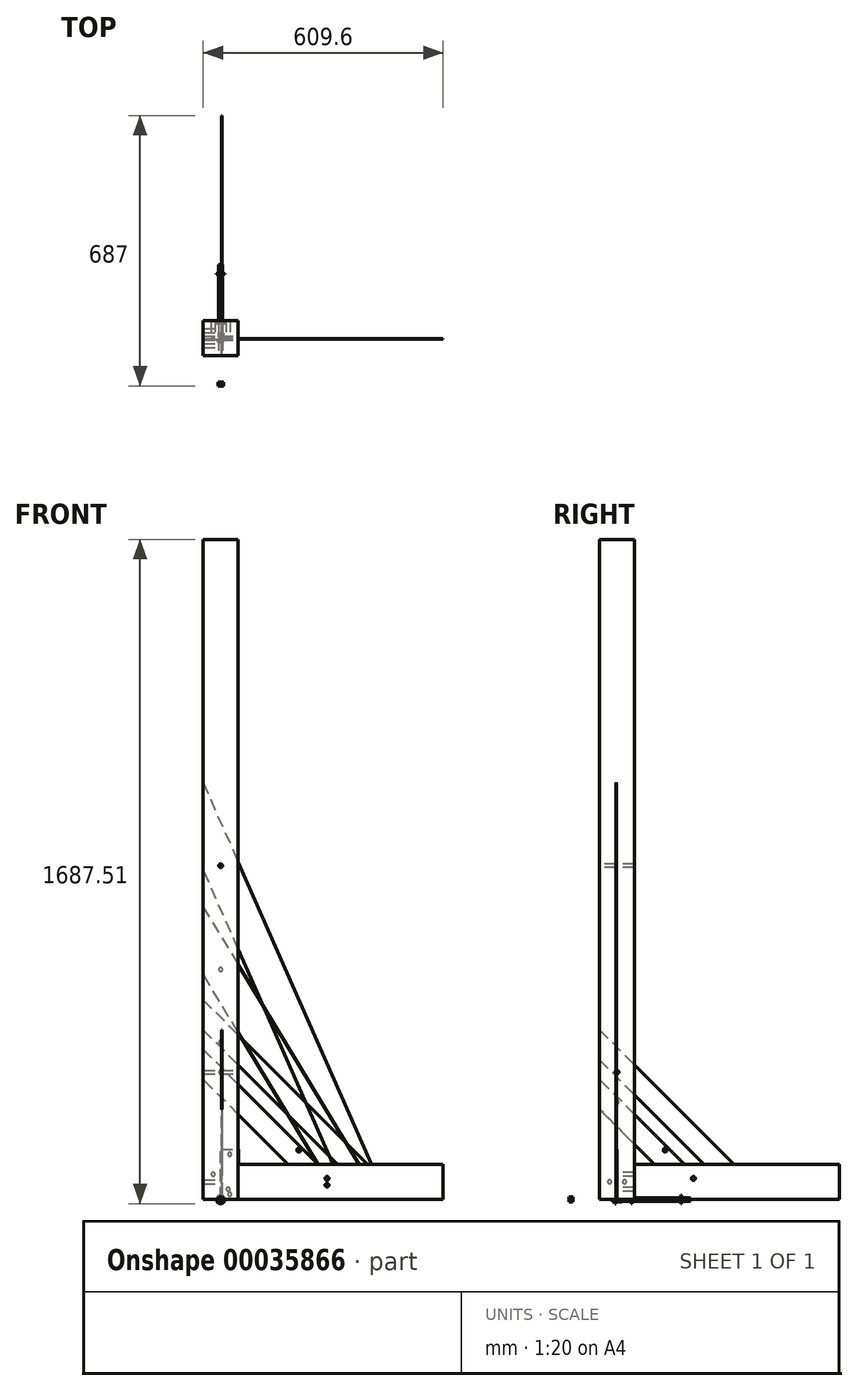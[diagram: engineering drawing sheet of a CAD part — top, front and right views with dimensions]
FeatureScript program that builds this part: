
annotation { "Feature Type Name" : "Feature", "Feature Type Description" : "" }
export const myFeature = defineFeature(function(context is Context, id is Id, definition is map)
    precondition{}
    {
        {
            assignVariable(context, id + "F0", {"name" : "mscthick", "anyValue" : 3.5});
        }
        {
            assignVariable(context, id + "F1", {"name" : "basethick", "anyValue" : 1.5});
        }
        {
            assignVariable(context, id + "F2", {"name" : "msc6", "anyValue" : 152.4 * mm});
        }
        {
            assignVariable(context, id + "F3", {"name" : "msc18", "anyValue" : 457.2 * mm});
        }
        {
            assignVariable(context, id + "F4", {"name" : "msc45", "anyValue" : 1143 * mm});
        }
        {
            assignVariable(context, id + "F5", {"name" : "msc24", "anyValue" : 609.6 * mm});
        }
        {
            assignVariable(context, id + "F6", {"name" : "msc30", "anyValue" : 762 * mm});
        }
        {
            assignVariable(context, id + "F7", {"name" : "msc66", "anyValue" : 1676.4 * mm});
        }
        {
            var Q0;
            Q0=qCreatedBy(makeId("Front.planeOp"),FACE);
            cPlane(context, id + "F8", {"entities" : qUnion([Q0]), "cplaneType" : CPlaneType.OFFSET, "offset" : (getVariable(context, 'mscthick') / 2) * mm, "width" : 152.4 * mm, "height" : 152.4 * mm});
        }
        {
            var Q0;
            Q0=qCreatedBy(makeId("Front.planeOp"),FACE);
            cPlane(context, id + "F9", {"entities" : qUnion([Q0]), "cplaneType" : CPlaneType.OFFSET, "offset" : (getVariable(context, 'mscthick') / 2) * mm, "oppositeDirection" : true, "width" : 152.4 * mm, "height" : 152.4 * mm});
        }
        {
            var Q0;
            Q0=qCreatedBy(makeId("Right.planeOp"),FACE);
            cPlane(context, id + "F10", {"entities" : qUnion([Q0]), "cplaneType" : CPlaneType.OFFSET, "offset" : (getVariable(context, 'mscthick') / 2) * mm, "width" : 152.4 * mm, "height" : 152.4 * mm});
        }
        {
            var Q0;
            Q0=qCreatedBy(makeId("Right.planeOp"),FACE);
            cPlane(context, id + "F11", {"entities" : qUnion([Q0]), "cplaneType" : CPlaneType.OFFSET, "offset" : (getVariable(context, 'mscthick') / 2) * mm, "oppositeDirection" : true, "width" : 152.4 * mm, "height" : 152.4 * mm});
        }
        {
            var Q0;
            Q0=qCreatedBy(id+"F8.planeOp",FACE);
            cPlane(context, id + "F12", {"entities" : qUnion([Q0]), "cplaneType" : CPlaneType.OFFSET, "offset" : (getVariable(context, 'basethick')) * mm, "width" : 152.4 * mm, "height" : 152.4 * mm});
        }
        {
            var Q0;
            Q0=qCreatedBy(id+"F9.planeOp",FACE);
            cPlane(context, id + "F13", {"entities" : qUnion([Q0]), "cplaneType" : CPlaneType.OFFSET, "offset" : (getVariable(context, 'basethick')) * mm, "oppositeDirection" : true, "width" : 152.4 * mm, "height" : 152.4 * mm});
        }
        {
            var Q0;
            Q0=qCreatedBy(id+"F10.planeOp",FACE);
            cPlane(context, id + "F14", {"entities" : qUnion([Q0]), "cplaneType" : CPlaneType.OFFSET, "offset" : (getVariable(context, 'basethick')) * mm, "width" : 152.4 * mm, "height" : 152.4 * mm});
        }
        {
            var Q0;
            Q0=qCreatedBy(makeId("Top.planeOp"),FACE);
            var sketch = newSketch(context, id + "F15", { "sketchPlane" : qUnion([Q0])});
            skLineSegment(sketch, "E0.rect.bottom", {"start": v(44.45, -44.45) * mm, "end": v(-44.45, -44.45) * mm});
            skLineSegment(sketch, "E0.rect.top", {"start": v(44.45, 44.45) * mm, "end": v(-44.45, 44.45) * mm});
            skLineSegment(sketch, "E0.rect.left", {"start": v(44.45, -44.45) * mm, "end": v(44.45, 44.45) * mm});
            skLineSegment(sketch, "E0.rect.right", {"start": v(-44.45, -44.45) * mm, "end": v(-44.45, 44.45) * mm});
            skPoint(sketch, "E0.rect.middle", {"position": v(0, 0) * mm});
            skSolve(sketch);
        }
        {
            var Q0;
            Q0=qCreatedBy(id+"F8.planeOp",FACE);
            var sketch = newSketch(context, id + "F16", { "sketchPlane" : qUnion([Q0])});
            skLineSegment(sketch, "E1", {"start": v(0, 0) * mm, "end": v(0, 88.9) * mm, "construction": true});
            skLineSegment(sketch, "E2.rect.bottom", {"start": v(44.45, 0) * mm, "end": v(-44.45, 0) * mm, "construction": true});
            skLineSegment(sketch, "E2.rect.top", {"start": v(44.45, 88.9) * mm, "end": v(-44.45, 88.9) * mm, "construction": true});
            skLineSegment(sketch, "E2.rect.left", {"start": v(44.45, 0) * mm, "end": v(44.45, 88.9) * mm, "construction": true});
            skLineSegment(sketch, "E2.rect.right", {"start": v(-44.45, 0) * mm, "end": v(-44.45, 88.9) * mm, "construction": true});
            skPoint(sketch, "E2.rect.middle", {"position": v(0, 44.45) * mm});
            skLineSegment(sketch, "E3.bottom", {"start": v(-44.45, 88.9) * mm, "end": v(-19.05, 88.9) * mm, "construction": true});
            skLineSegment(sketch, "E3.top", {"start": v(-44.45, 63.5) * mm, "end": v(-19.05, 63.5) * mm, "construction": true});
            skLineSegment(sketch, "E3.left", {"start": v(-44.45, 88.9) * mm, "end": v(-44.45, 63.5) * mm, "construction": true});
            skLineSegment(sketch, "E3.right", {"start": v(-19.05, 88.9) * mm, "end": v(-19.05, 63.5) * mm, "construction": true});
            skLineSegment(sketch, "E4.bottom", {"start": v(44.45, 0) * mm, "end": v(19.05, 0) * mm, "construction": true});
            skLineSegment(sketch, "E4.top", {"start": v(44.45, 25.4) * mm, "end": v(19.05, 25.4) * mm, "construction": true});
            skLineSegment(sketch, "E4.left", {"start": v(44.45, 0) * mm, "end": v(44.45, 25.4) * mm, "construction": true});
            skLineSegment(sketch, "E4.right", {"start": v(19.05, 0) * mm, "end": v(19.05, 25.4) * mm, "construction": true});
            skCircle(sketch, "E5", {"center": v(-19.05, 63.5) * mm, "radius": 4.76 * mm});
            skCircle(sketch, "E6", {"center": v(19.05, 25.4) * mm, "radius": 4.76 * mm});
            skSolve(sketch);
        }
        {
            var Q0;
            Q0=qCreatedBy(id+"F10.planeOp",FACE);
            var sketch = newSketch(context, id + "F17", { "sketchPlane" : qUnion([Q0])});
            skLineSegment(sketch, "E7", {"start": v(0, 0) * mm, "end": v(0, 88.9) * mm, "construction": true});
            skLineSegment(sketch, "E8.rect.bottom", {"start": v(44.45, 0) * mm, "end": v(-44.45, 0) * mm, "construction": true});
            skLineSegment(sketch, "E8.rect.top", {"start": v(44.45, 88.9) * mm, "end": v(-44.45, 88.9) * mm, "construction": true});
            skLineSegment(sketch, "E8.rect.left", {"start": v(44.45, 0) * mm, "end": v(44.45, 88.9) * mm, "construction": true});
            skLineSegment(sketch, "E8.rect.right", {"start": v(-44.45, 0) * mm, "end": v(-44.45, 88.9) * mm, "construction": true});
            skPoint(sketch, "E8.rect.middle", {"position": v(0, 44.45) * mm});
            skLineSegment(sketch, "E9", {"start": v(-44.45, 44.45) * mm, "end": v(-19.05, 44.45) * mm, "construction": true});
            skPoint(sketch, "E9.endSnap0", {"position": v(44.45, 44.45) * mm});
            skLineSegment(sketch, "E10", {"start": v(-19.05, 44.45) * mm, "end": v(19.05, 44.45) * mm, "construction": true});
            skLineSegment(sketch, "E11", {"start": v(19.05, 44.45) * mm, "end": v(44.45, 44.45) * mm, "construction": true});
            skCircle(sketch, "E12", {"center": v(-19.05, 44.45) * mm, "radius": 4.76 * mm});
            skCircle(sketch, "E13", {"center": v(19.05, 44.45) * mm, "radius": 4.76 * mm});
            skSolve(sketch);
        }
        {
            var Q0;
            Q0=qCreatedBy(id+"F8.planeOp",FACE);
            var sketch = newSketch(context, id + "F18", { "sketchPlane" : qUnion([Q0])});
            skLineSegment(sketch, "E14", {"start": v(0, 0) * mm, "end": v(-44.45, 0) * mm, "construction": true});
            skLineSegment(sketch, "E15", {"start": v(-44.45, 0) * mm, "end": v(-44.45, 88.9) * mm, "construction": true});
            skLineSegment(sketch, "E16.bottom", {"start": v(-44.45, 0) * mm, "end": v(565.15, 0) * mm});
            skLineSegment(sketch, "E16.top", {"start": v(-44.45, 88.9) * mm, "end": v(565.15, 88.9) * mm});
            skLineSegment(sketch, "E16.left", {"start": v(-44.45, 0) * mm, "end": v(-44.45, 88.9) * mm});
            skLineSegment(sketch, "E16.right", {"start": v(565.15, 0) * mm, "end": v(565.15, 88.9) * mm});
            skLineSegment(sketch, "E17.bottom", {"start": v(-44.45, 88.9) * mm, "end": v(-19.05, 88.9) * mm, "construction": true});
            skLineSegment(sketch, "E17.top", {"start": v(-44.45, 63.5) * mm, "end": v(-19.05, 63.5) * mm, "construction": true});
            skLineSegment(sketch, "E17.left", {"start": v(-44.45, 88.9) * mm, "end": v(-44.45, 63.5) * mm, "construction": true});
            skLineSegment(sketch, "E17.right", {"start": v(-19.05, 88.9) * mm, "end": v(-19.05, 63.5) * mm, "construction": true});
            skLineSegment(sketch, "E18", {"start": v(-44.45, 88.9) * mm, "end": v(44.45, 0) * mm, "construction": true});
            skLineSegment(sketch, "E19.bottom", {"start": v(44.45, 0) * mm, "end": v(19.05, 0) * mm, "construction": true});
            skLineSegment(sketch, "E19.top", {"start": v(44.45, 25.4) * mm, "end": v(19.05, 25.4) * mm, "construction": true});
            skLineSegment(sketch, "E19.left", {"start": v(44.45, 0) * mm, "end": v(44.45, 25.4) * mm, "construction": true});
            skLineSegment(sketch, "E19.right", {"start": v(19.05, 0) * mm, "end": v(19.05, 25.4) * mm, "construction": true});
            skCircle(sketch, "E20", {"center": v(-19.05, 63.5) * mm, "radius": 4.76 * mm});
            skCircle(sketch, "E21", {"center": v(19.05, 25.4) * mm, "radius": 4.76 * mm});
            skSolve(sketch);
        }
        {
            var Q0;
            Q0=qCreatedBy(id+"F10.planeOp",FACE);
            var sketch = newSketch(context, id + "F19", { "sketchPlane" : qUnion([Q0])});
            skLineSegment(sketch, "E22", {"start": v(0, 0) * mm, "end": v(-44.45, 0) * mm, "construction": true});
            skLineSegment(sketch, "E23", {"start": v(-44.45, 0) * mm, "end": v(-44.45, 88.9) * mm, "construction": true});
            skLineSegment(sketch, "E24.bottom", {"start": v(-44.45, 88.9) * mm, "end": v(565.15, 88.9) * mm});
            skLineSegment(sketch, "E24.top", {"start": v(-44.45, 0) * mm, "end": v(565.15, 0) * mm});
            skLineSegment(sketch, "E24.left", {"start": v(-44.45, 88.9) * mm, "end": v(-44.45, 0) * mm});
            skLineSegment(sketch, "E24.right", {"start": v(565.15, 88.9) * mm, "end": v(565.15, 0) * mm});
            skLineSegment(sketch, "E25", {"start": v(0, 0) * mm, "end": v(0, 88.9) * mm, "construction": true});
            skLineSegment(sketch, "E26", {"start": v(-44.45, 44.45) * mm, "end": v(-19.05, 44.45) * mm, "construction": true});
            skLineSegment(sketch, "E27", {"start": v(-19.05, 44.45) * mm, "end": v(19.05, 44.45) * mm, "construction": true});
            skLineSegment(sketch, "E28", {"start": v(19.05, 44.45) * mm, "end": v(44.45, 44.45) * mm, "construction": true});
            skCircle(sketch, "E29", {"center": v(-19.05, 44.45) * mm, "radius": 4.76 * mm});
            skCircle(sketch, "E30", {"center": v(19.05, 44.45) * mm, "radius": 4.76 * mm});
            skSolve(sketch);
        }
        {
            var Q0;
            Q0=qCreatedBy(id+"F14.planeOp",FACE);
            var sketch = newSketch(context, id + "F20", { "sketchPlane" : qUnion([Q0])});
            skLineSegment(sketch, "E31", {"start": v(171.45, 0) * mm, "end": v(-44.45, 0) * mm, "construction": true});
            skLineSegment(sketch, "E32", {"start": v(-44.45, 0) * mm, "end": v(-44.45, 304.8) * mm, "construction": true});
            skLineSegment(sketch, "E33", {"start": v(-44.45, 304.8) * mm, "end": v(171.45, 88.9) * mm, "construction": true});
            skLineSegment(sketch, "E34", {"start": v(171.45, 88.9) * mm, "end": v(171.45, 0) * mm, "construction": true});
            skLineSegment(sketch, "E35", {"start": v(171.45, 0) * mm, "end": v(260.35, 0) * mm, "construction": true});
            skLineSegment(sketch, "E36", {"start": v(63.5, 196.85) * mm, "end": v(126.36, 259.71) * mm, "construction": true});
            skLineSegment(sketch, "E37", {"start": v(126.36, 259.71) * mm, "end": v(-44.45, 430.52) * mm, "construction": true});
            skLineSegment(sketch, "E38", {"start": v(-44.45, 304.8) * mm, "end": v(-44.45, 430.52) * mm});
            skLineSegment(sketch, "E39", {"start": v(-44.45, 430.52) * mm, "end": v(297.17, 88.9) * mm});
            skLineSegment(sketch, "E40", {"start": v(297.17, 88.9) * mm, "end": v(171.45, 88.9) * mm});
            skLineSegment(sketch, "E41", {"start": v(171.45, 88.9) * mm, "end": v(-44.45, 304.8) * mm});
            skLineSegment(sketch, "E42", {"start": v(-44.45, 367.66) * mm, "end": v(234.31, 88.9) * mm, "construction": true});
            skLineSegment(sketch, "E43", {"start": v(0, 0) * mm, "end": v(0, 365.42) * mm, "construction": true});
            skLineSegment(sketch, "E44.rect.bottom", {"start": v(25.4, 297.81) * mm, "end": v(-25.4, 297.81) * mm, "construction": true});
            skLineSegment(sketch, "E44.rect.top", {"start": v(25.4, 348.61) * mm, "end": v(-25.4, 348.61) * mm, "construction": true});
            skLineSegment(sketch, "E44.rect.left", {"start": v(25.4, 297.81) * mm, "end": v(25.4, 348.61) * mm, "construction": true});
            skLineSegment(sketch, "E44.rect.right", {"start": v(-25.4, 297.81) * mm, "end": v(-25.4, 348.61) * mm, "construction": true});
            skPoint(sketch, "E44.rect.middle", {"position": v(0, 323.21) * mm});
            skCircle(sketch, "E45", {"center": v(0, 323.21) * mm, "radius": 4.76 * mm});
            skSolve(sketch);
        }
        {
            var Q0;
            Q0=qCreatedBy(makeId("Right.planeOp"),FACE);
            var sketch = newSketch(context, id + "F21", { "sketchPlane" : qUnion([Q0])});
            skLineSegment(sketch, "E46", {"start": v(171.45, 0) * mm, "end": v(-44.45, 0) * mm, "construction": true});
            skLineSegment(sketch, "E47", {"start": v(-44.45, 0) * mm, "end": v(-44.45, 304.8) * mm, "construction": true});
            skLineSegment(sketch, "E48", {"start": v(-44.45, 304.8) * mm, "end": v(171.45, 88.9) * mm, "construction": true});
            skLineSegment(sketch, "E49", {"start": v(171.45, 88.9) * mm, "end": v(171.45, 0) * mm, "construction": true});
            skLineSegment(sketch, "E50", {"start": v(171.45, 0) * mm, "end": v(260.35, 0) * mm, "construction": true});
            skLineSegment(sketch, "E51", {"start": v(63.5, 196.85) * mm, "end": v(126.36, 259.71) * mm, "construction": true});
            skLineSegment(sketch, "E52", {"start": v(126.36, 259.71) * mm, "end": v(-44.45, 430.52) * mm, "construction": true});
            skLineSegment(sketch, "E53", {"start": v(-44.45, 304.8) * mm, "end": v(-44.45, 430.52) * mm, "construction": true});
            skLineSegment(sketch, "E54", {"start": v(-44.45, 430.52) * mm, "end": v(297.17, 88.9) * mm, "construction": true});
            skLineSegment(sketch, "E55", {"start": v(297.17, 88.9) * mm, "end": v(171.45, 88.9) * mm, "construction": true});
            skLineSegment(sketch, "E56", {"start": v(171.45, 88.9) * mm, "end": v(-44.45, 304.8) * mm, "construction": true});
            skLineSegment(sketch, "E57", {"start": v(-44.45, 367.66) * mm, "end": v(234.31, 88.9) * mm, "construction": true});
            skLineSegment(sketch, "E58", {"start": v(0, 0) * mm, "end": v(0, 142.77) * mm, "construction": true});
            skLineSegment(sketch, "E59.rect.bottom", {"start": v(25.4, 297.81) * mm, "end": v(-25.4, 297.81) * mm, "construction": true});
            skLineSegment(sketch, "E59.rect.top", {"start": v(25.4, 348.61) * mm, "end": v(-25.4, 348.61) * mm, "construction": true});
            skLineSegment(sketch, "E59.rect.left", {"start": v(25.4, 297.81) * mm, "end": v(25.4, 348.61) * mm, "construction": true});
            skLineSegment(sketch, "E59.rect.right", {"start": v(-25.4, 297.81) * mm, "end": v(-25.4, 348.61) * mm, "construction": true});
            skPoint(sketch, "E59.rect.middle", {"position": v(0, 323.21) * mm});
            skCircle(sketch, "E60", {"center": v(0, 323.21) * mm, "radius": 4.76 * mm});
            skSolve(sketch);
        }
        {
            var Q0;
            Q0=qCreatedBy(makeId("Front.planeOp"),FACE);
            var sketch = newSketch(context, id + "F22", { "sketchPlane" : qUnion([Q0])});
            skLineSegment(sketch, "E61", {"start": v(95.25, 0) * mm, "end": v(-44.45, 0) * mm, "construction": true});
            skLineSegment(sketch, "E62", {"start": v(-44.45, 0) * mm, "end": v(-44.45, 228.6) * mm, "construction": true});
            skLineSegment(sketch, "E63", {"start": v(-44.45, 228.6) * mm, "end": v(95.25, 88.9) * mm, "construction": true});
            skLineSegment(sketch, "E64", {"start": v(95.25, 88.9) * mm, "end": v(95.25, 0) * mm, "construction": true});
            skLineSegment(sketch, "E65", {"start": v(95.25, 0) * mm, "end": v(184.15, 0) * mm, "construction": true});
            skLineSegment(sketch, "E66", {"start": v(201.17, 108.7) * mm, "end": v(-44.45, 354.32) * mm, "construction": true});
            skLineSegment(sketch, "E67", {"start": v(-44.45, 228.6) * mm, "end": v(-44.45, 354.32) * mm, "construction": true});
            skLineSegment(sketch, "E68", {"start": v(-44.45, 354.32) * mm, "end": v(220.97, 88.9) * mm, "construction": true});
            skLineSegment(sketch, "E69", {"start": v(220.97, 88.9) * mm, "end": v(95.25, 88.9) * mm, "construction": true});
            skLineSegment(sketch, "E70", {"start": v(95.25, 88.9) * mm, "end": v(-44.45, 228.6) * mm, "construction": true});
            skLineSegment(sketch, "E71", {"start": v(-44.45, 291.46) * mm, "end": v(158.11, 88.9) * mm, "construction": true});
            skLineSegment(sketch, "E72", {"start": v(0, 0) * mm, "end": v(0, 309.87) * mm, "construction": true});
            skLineSegment(sketch, "E73.rect.bottom", {"start": v(25.4, 221.61) * mm, "end": v(-25.4, 221.61) * mm, "construction": true});
            skLineSegment(sketch, "E73.rect.top", {"start": v(25.4, 272.41) * mm, "end": v(-25.4, 272.41) * mm, "construction": true});
            skLineSegment(sketch, "E73.rect.left", {"start": v(25.4, 221.61) * mm, "end": v(25.4, 272.41) * mm, "construction": true});
            skLineSegment(sketch, "E73.rect.right", {"start": v(-25.4, 221.61) * mm, "end": v(-25.4, 272.41) * mm, "construction": true});
            skPoint(sketch, "E73.rect.middle", {"position": v(0, 247.01) * mm});
            skCircle(sketch, "E74", {"center": v(0, 247.01) * mm, "radius": 4.76 * mm});
            skSolve(sketch);
        }
        {
            var Q0;
            Q0=qCreatedBy(id+"F8.planeOp",FACE);
            var sketch = newSketch(context, id + "F23", { "sketchPlane" : qUnion([Q0])});
            skLineSegment(sketch, "E75", {"start": v(171.45, 0) * mm, "end": v(-44.45, 0) * mm, "construction": true});
            skLineSegment(sketch, "E76", {"start": v(-44.45, 0) * mm, "end": v(-44.45, 304.8) * mm, "construction": true});
            skLineSegment(sketch, "E77", {"start": v(-44.45, 304.8) * mm, "end": v(171.45, 88.9) * mm, "construction": true});
            skLineSegment(sketch, "E78", {"start": v(171.45, 88.9) * mm, "end": v(171.45, 0) * mm, "construction": true});
            skLineSegment(sketch, "E79", {"start": v(171.45, 0) * mm, "end": v(260.35, 0) * mm, "construction": true});
            skLineSegment(sketch, "E80", {"start": v(63.5, 196.85) * mm, "end": v(126.36, 259.71) * mm, "construction": true});
            skLineSegment(sketch, "E81", {"start": v(126.36, 259.71) * mm, "end": v(-44.45, 430.52) * mm, "construction": true});
            skLineSegment(sketch, "E82", {"start": v(-44.45, 304.8) * mm, "end": v(-44.45, 430.52) * mm});
            skLineSegment(sketch, "E83", {"start": v(-44.45, 430.52) * mm, "end": v(297.17, 88.9) * mm});
            skLineSegment(sketch, "E84", {"start": v(297.17, 88.9) * mm, "end": v(171.45, 88.9) * mm});
            skLineSegment(sketch, "E85", {"start": v(171.45, 88.9) * mm, "end": v(-44.45, 304.8) * mm});
            skLineSegment(sketch, "E86", {"start": v(-44.45, 367.66) * mm, "end": v(234.31, 88.9) * mm, "construction": true});
            skLineSegment(sketch, "E87", {"start": v(0, 0) * mm, "end": v(0, 594.1) * mm, "construction": true});
            skLineSegment(sketch, "E88.rect.bottom", {"start": v(25.4, 297.81) * mm, "end": v(-25.4, 297.81) * mm, "construction": true});
            skLineSegment(sketch, "E88.rect.top", {"start": v(25.4, 348.61) * mm, "end": v(-25.4, 348.61) * mm, "construction": true});
            skLineSegment(sketch, "E88.rect.left", {"start": v(25.4, 297.81) * mm, "end": v(25.4, 348.61) * mm, "construction": true});
            skLineSegment(sketch, "E88.rect.right", {"start": v(-25.4, 297.81) * mm, "end": v(-25.4, 348.61) * mm, "construction": true});
            skPoint(sketch, "E88.rect.middle", {"position": v(0, 323.21) * mm});
            skCircle(sketch, "E89", {"center": v(0, 323.21) * mm, "radius": 4.76 * mm});
            skSolve(sketch);
        }
        {
            var Q0;
            Q0=qCreatedBy(id+"F14.planeOp",FACE);
            var sketch = newSketch(context, id + "F24", { "sketchPlane" : qUnion([Q0])});
            skLineSegment(sketch, "E90", {"start": v(95.25, 0) * mm, "end": v(-44.45, 0) * mm, "construction": true});
            skLineSegment(sketch, "E91", {"start": v(-44.45, 0) * mm, "end": v(-44.45, 228.6) * mm, "construction": true});
            skLineSegment(sketch, "E92", {"start": v(-44.45, 228.6) * mm, "end": v(95.25, 88.9) * mm, "construction": true});
            skLineSegment(sketch, "E93", {"start": v(95.25, 88.9) * mm, "end": v(95.25, 0) * mm, "construction": true});
            skLineSegment(sketch, "E94", {"start": v(95.25, 0) * mm, "end": v(184.15, 0) * mm, "construction": true});
            skLineSegment(sketch, "E95", {"start": v(201.17, 108.7) * mm, "end": v(-44.45, 354.32) * mm, "construction": true});
            skLineSegment(sketch, "E96", {"start": v(-44.45, 228.6) * mm, "end": v(-44.45, 354.32) * mm});
            skLineSegment(sketch, "E97", {"start": v(-44.45, 354.32) * mm, "end": v(220.97, 88.9) * mm});
            skLineSegment(sketch, "E98", {"start": v(220.97, 88.9) * mm, "end": v(95.25, 88.9) * mm});
            skLineSegment(sketch, "E99", {"start": v(95.25, 88.9) * mm, "end": v(-44.45, 228.6) * mm});
            skLineSegment(sketch, "E100", {"start": v(-44.45, 291.46) * mm, "end": v(158.11, 88.9) * mm, "construction": true});
            skLineSegment(sketch, "E101", {"start": v(0, 0) * mm, "end": v(0, 309.87) * mm, "construction": true});
            skLineSegment(sketch, "E102.rect.bottom", {"start": v(25.4, 221.61) * mm, "end": v(-25.4, 221.61) * mm, "construction": true});
            skLineSegment(sketch, "E102.rect.top", {"start": v(25.4, 272.41) * mm, "end": v(-25.4, 272.41) * mm, "construction": true});
            skLineSegment(sketch, "E102.rect.left", {"start": v(25.4, 221.61) * mm, "end": v(25.4, 272.41) * mm, "construction": true});
            skLineSegment(sketch, "E102.rect.right", {"start": v(-25.4, 221.61) * mm, "end": v(-25.4, 272.41) * mm, "construction": true});
            skPoint(sketch, "E102.rect.middle", {"position": v(0, 247.01) * mm});
            skCircle(sketch, "E103", {"center": v(0, 247.01) * mm, "radius": 4.76 * mm});
            skSolve(sketch);
        }
        {
            var Q0;
            Q0=qCreatedBy(makeId("Front.planeOp"),FACE);
            var sketch = newSketch(context, id + "F25", { "sketchPlane" : qUnion([Q0])});
            skLineSegment(sketch, "E104", {"start": v(0, 0) * mm, "end": v(-44.45, 0) * mm, "construction": true});
            skLineSegment(sketch, "E105", {"start": v(-44.45, 0) * mm, "end": v(-44.45, 304.8) * mm, "construction": true});
            skLineSegment(sketch, "E106", {"start": v(-44.45, 0) * mm, "end": v(260.35, 0) * mm, "construction": true});
            skLineSegment(sketch, "E107", {"start": v(260.35, 0) * mm, "end": v(171.45, 0) * mm, "construction": true});
            skLineSegment(sketch, "E108", {"start": v(171.45, 0) * mm, "end": v(171.45, 88.9) * mm, "construction": true});
            skLineSegment(sketch, "E109", {"start": v(171.45, 88.9) * mm, "end": v(-44.45, 304.8) * mm, "construction": true});
            skLineSegment(sketch, "E110", {"start": v(-44.45, 304.8) * mm, "end": v(-44.45, 430.52) * mm, "construction": true});
            skLineSegment(sketch, "E111", {"start": v(-44.45, 430.52) * mm, "end": v(297.17, 88.9) * mm, "construction": true});
            skLineSegment(sketch, "E112", {"start": v(297.17, 88.9) * mm, "end": v(171.45, 88.9) * mm, "construction": true});
            skLineSegment(sketch, "E113", {"start": v(-44.45, 367.66) * mm, "end": v(234.31, 88.9) * mm, "construction": true});
            skLineSegment(sketch, "E114", {"start": v(0, 0) * mm, "end": v(0, 386.07) * mm, "construction": true});
            skPoint(sketch, "E115.rect.middle", {"position": v(0, 323.21) * mm});
            skCircle(sketch, "E116", {"center": v(0, 323.21) * mm, "radius": 4.76 * mm});
            skSolve(sketch);
        }
        {
            var Q0;
            Q0=qCreatedBy(makeId("Right.planeOp"),FACE);
            var sketch = newSketch(context, id + "F26", { "sketchPlane" : qUnion([Q0])});
            skLineSegment(sketch, "E117", {"start": v(95.25, 0) * mm, "end": v(-44.45, 0) * mm, "construction": true});
            skLineSegment(sketch, "E118", {"start": v(-44.45, 0) * mm, "end": v(-44.45, 228.6) * mm, "construction": true});
            skLineSegment(sketch, "E119", {"start": v(-44.45, 228.6) * mm, "end": v(95.25, 88.9) * mm, "construction": true});
            skLineSegment(sketch, "E120", {"start": v(95.25, 88.9) * mm, "end": v(95.25, 0) * mm, "construction": true});
            skLineSegment(sketch, "E121", {"start": v(95.25, 0) * mm, "end": v(184.15, 0) * mm, "construction": true});
            skLineSegment(sketch, "E122", {"start": v(201.17, 108.7) * mm, "end": v(-44.45, 354.32) * mm, "construction": true});
            skLineSegment(sketch, "E123", {"start": v(-44.45, 228.6) * mm, "end": v(-44.45, 354.32) * mm, "construction": true});
            skLineSegment(sketch, "E124", {"start": v(-44.45, 354.32) * mm, "end": v(220.97, 88.9) * mm, "construction": true});
            skLineSegment(sketch, "E125", {"start": v(220.97, 88.9) * mm, "end": v(95.25, 88.9) * mm, "construction": true});
            skLineSegment(sketch, "E126", {"start": v(95.25, 88.9) * mm, "end": v(-44.45, 228.6) * mm, "construction": true});
            skLineSegment(sketch, "E127", {"start": v(-44.45, 291.46) * mm, "end": v(158.11, 88.9) * mm, "construction": true});
            skLineSegment(sketch, "E128", {"start": v(0, 0) * mm, "end": v(0, 309.87) * mm, "construction": true});
            skLineSegment(sketch, "E129.rect.bottom", {"start": v(25.4, 221.61) * mm, "end": v(-25.4, 221.61) * mm, "construction": true});
            skLineSegment(sketch, "E129.rect.top", {"start": v(25.4, 272.41) * mm, "end": v(-25.4, 272.41) * mm, "construction": true});
            skLineSegment(sketch, "E129.rect.left", {"start": v(25.4, 221.61) * mm, "end": v(25.4, 272.41) * mm, "construction": true});
            skLineSegment(sketch, "E129.rect.right", {"start": v(-25.4, 221.61) * mm, "end": v(-25.4, 272.41) * mm, "construction": true});
            skPoint(sketch, "E129.rect.middle", {"position": v(0, 247.01) * mm});
            skCircle(sketch, "E130", {"center": v(0, 247.01) * mm, "radius": 4.76 * mm});
            skSolve(sketch);
        }
        {
            var Q0;
            Q0=qCreatedBy(id+"F8.planeOp",FACE);
            var sketch = newSketch(context, id + "F27", { "sketchPlane" : qUnion([Q0])});
            skLineSegment(sketch, "E131", {"start": v(-44.45, 0) * mm, "end": v(336.55, 0) * mm, "construction": true});
            skLineSegment(sketch, "E132", {"start": v(247.65, 0) * mm, "end": v(247.65, 88.9) * mm, "construction": true});
            skLineSegment(sketch, "E133", {"start": v(-44.45, 0) * mm, "end": v(-44.45, 381) * mm, "construction": true});
            skLineSegment(sketch, "E134", {"start": v(-44.45, 381) * mm, "end": v(247.65, 88.9) * mm});
            skLineSegment(sketch, "E135", {"start": v(-44.45, 506.72) * mm, "end": v(373.37, 88.9) * mm});
            skLineSegment(sketch, "E136", {"start": v(373.37, 88.9) * mm, "end": v(247.65, 88.9) * mm});
            skLineSegment(sketch, "E137", {"start": v(-44.45, 381) * mm, "end": v(-44.45, 506.72) * mm});
            skLineSegment(sketch, "E138", {"start": v(0, 0) * mm, "end": v(0, 462.27) * mm, "construction": true});
            skLineSegment(sketch, "E139", {"start": v(-44.45, 443.86) * mm, "end": v(310.51, 88.9) * mm, "construction": true});
            skLineSegment(sketch, "E140.rect.bottom", {"start": v(25.4, 374.01) * mm, "end": v(-25.4, 374.01) * mm, "construction": true});
            skLineSegment(sketch, "E140.rect.top", {"start": v(25.4, 424.81) * mm, "end": v(-25.4, 424.81) * mm, "construction": true});
            skLineSegment(sketch, "E140.rect.left", {"start": v(25.4, 374.01) * mm, "end": v(25.4, 424.81) * mm, "construction": true});
            skLineSegment(sketch, "E140.rect.right", {"start": v(-25.4, 374.01) * mm, "end": v(-25.4, 424.81) * mm, "construction": true});
            skPoint(sketch, "E140.rect.middle", {"position": v(0, 399.41) * mm});
            skCircle(sketch, "E141", {"center": v(0, 399.41) * mm, "radius": 4.76 * mm});
            skSolve(sketch);
        }
        {
            var Q0;
            Q0=qCreatedBy(makeId("Front.planeOp"),FACE);
            var sketch = newSketch(context, id + "F28", { "sketchPlane" : qUnion([Q0])});
            skLineSegment(sketch, "E142", {"start": v(-44.45, 0) * mm, "end": v(336.55, 0) * mm, "construction": true});
            skLineSegment(sketch, "E143", {"start": v(247.65, 0) * mm, "end": v(247.65, 88.9) * mm, "construction": true});
            skLineSegment(sketch, "E144", {"start": v(-44.45, 0) * mm, "end": v(-44.45, 381) * mm, "construction": true});
            skLineSegment(sketch, "E145", {"start": v(-44.45, 381) * mm, "end": v(247.65, 88.9) * mm, "construction": true});
            skLineSegment(sketch, "E146", {"start": v(-44.45, 506.72) * mm, "end": v(373.37, 88.9) * mm, "construction": true});
            skLineSegment(sketch, "E147", {"start": v(373.37, 88.9) * mm, "end": v(247.65, 88.9) * mm, "construction": true});
            skLineSegment(sketch, "E148", {"start": v(-44.45, 381) * mm, "end": v(-44.45, 506.72) * mm, "construction": true});
            skLineSegment(sketch, "E149", {"start": v(0, 0) * mm, "end": v(0, 462.27) * mm, "construction": true});
            skLineSegment(sketch, "E150", {"start": v(-44.45, 443.86) * mm, "end": v(310.51, 88.9) * mm, "construction": true});
            skLineSegment(sketch, "E151.rect.bottom", {"start": v(25.4, 374.01) * mm, "end": v(-25.4, 374.01) * mm, "construction": true});
            skLineSegment(sketch, "E151.rect.top", {"start": v(25.4, 424.81) * mm, "end": v(-25.4, 424.81) * mm, "construction": true});
            skLineSegment(sketch, "E151.rect.left", {"start": v(25.4, 374.01) * mm, "end": v(25.4, 424.81) * mm, "construction": true});
            skLineSegment(sketch, "E151.rect.right", {"start": v(-25.4, 374.01) * mm, "end": v(-25.4, 424.81) * mm, "construction": true});
            skPoint(sketch, "E151.rect.middle", {"position": v(0, 399.41) * mm});
            skCircle(sketch, "E152", {"center": v(-25.4, 424.81) * mm, "radius": 4.76 * mm, "construction": true});
            skCircle(sketch, "E153", {"center": v(25.4, 374.01) * mm, "radius": 4.76 * mm, "construction": true});
            skCircle(sketch, "E154", {"center": v(-25.4, 374.01) * mm, "radius": 4.76 * mm, "construction": true});
            skCircle(sketch, "E155", {"center": v(25.4, 424.81) * mm, "radius": 4.76 * mm, "construction": true});
            skCircle(sketch, "E156", {"center": v(0, 399.41) * mm, "radius": 4.76 * mm});
            skSolve(sketch);
        }
        {
            var Q0;
            Q0=qCreatedBy(id+"F12.planeOp",FACE);
            var sketch = newSketch(context, id + "F29", { "sketchPlane" : qUnion([Q0])});
            skLineSegment(sketch, "E157", {"start": v(247.65, 0) * mm, "end": v(-44.45, 0) * mm, "construction": true});
            skLineSegment(sketch, "E158", {"start": v(-44.45, 0) * mm, "end": v(-44.45, 571.5) * mm, "construction": true});
            skLineSegment(sketch, "E159", {"start": v(-44.45, 571.5) * mm, "end": v(247.65, 88.9) * mm, "construction": true});
            skLineSegment(sketch, "E160", {"start": v(247.65, 88.9) * mm, "end": v(247.65, 0) * mm, "construction": true});
            skLineSegment(sketch, "E161", {"start": v(247.65, 0) * mm, "end": v(336.55, 0) * mm, "construction": true});
            skLineSegment(sketch, "E162", {"start": v(250.83, 255.33) * mm, "end": v(-44.45, 743.19) * mm, "construction": true});
            skLineSegment(sketch, "E163", {"start": v(-44.45, 571.5) * mm, "end": v(-44.45, 743.19) * mm});
            skLineSegment(sketch, "E164", {"start": v(-44.45, 743.19) * mm, "end": v(351.57, 88.9) * mm});
            skLineSegment(sketch, "E165", {"start": v(351.57, 88.9) * mm, "end": v(247.65, 88.9) * mm});
            skLineSegment(sketch, "E166", {"start": v(247.65, 88.9) * mm, "end": v(-44.45, 571.5) * mm});
            skLineSegment(sketch, "E167", {"start": v(-44.45, 657.34) * mm, "end": v(299.6, 88.9) * mm, "construction": true});
            skLineSegment(sketch, "E168", {"start": v(0, 0) * mm, "end": v(0, 669.75) * mm, "construction": true});
            skLineSegment(sketch, "E169.rect.bottom", {"start": v(25.4, 541.94) * mm, "end": v(-25.4, 541.94) * mm, "construction": true});
            skLineSegment(sketch, "E169.rect.top", {"start": v(25.4, 625.87) * mm, "end": v(-25.4, 625.87) * mm, "construction": true});
            skLineSegment(sketch, "E169.rect.left", {"start": v(25.4, 541.94) * mm, "end": v(25.4, 625.87) * mm, "construction": true});
            skLineSegment(sketch, "E169.rect.right", {"start": v(-25.4, 541.94) * mm, "end": v(-25.4, 625.87) * mm, "construction": true});
            skPoint(sketch, "E169.rect.middle", {"position": v(0, 583.9) * mm});
            skCircle(sketch, "E170", {"center": v(0, 583.9) * mm, "radius": 4.76 * mm});
            skSolve(sketch);
        }
        {
            var Q0;
            Q0=qCreatedBy(makeId("Front.planeOp"),FACE);
            var sketch = newSketch(context, id + "F30", { "sketchPlane" : qUnion([Q0])});
            skLineSegment(sketch, "E171", {"start": v(247.65, 0) * mm, "end": v(-44.45, 0) * mm, "construction": true});
            skLineSegment(sketch, "E172", {"start": v(-44.45, 0) * mm, "end": v(-44.45, 571.5) * mm, "construction": true});
            skLineSegment(sketch, "E173", {"start": v(-44.45, 571.5) * mm, "end": v(247.65, 88.9) * mm, "construction": true});
            skLineSegment(sketch, "E174", {"start": v(247.65, 88.9) * mm, "end": v(247.65, 0) * mm, "construction": true});
            skLineSegment(sketch, "E175", {"start": v(247.65, 0) * mm, "end": v(336.55, 0) * mm, "construction": true});
            skLineSegment(sketch, "E176", {"start": v(250.83, 255.33) * mm, "end": v(-44.45, 743.19) * mm, "construction": true});
            skLineSegment(sketch, "E177", {"start": v(-44.45, 571.5) * mm, "end": v(-44.45, 743.19) * mm, "construction": true});
            skLineSegment(sketch, "E178", {"start": v(-44.45, 743.19) * mm, "end": v(351.57, 88.9) * mm, "construction": true});
            skLineSegment(sketch, "E179", {"start": v(351.57, 88.9) * mm, "end": v(247.65, 88.9) * mm, "construction": true});
            skLineSegment(sketch, "E180", {"start": v(247.65, 88.9) * mm, "end": v(-44.45, 571.5) * mm, "construction": true});
            skLineSegment(sketch, "E181", {"start": v(-44.45, 657.34) * mm, "end": v(299.6, 88.9) * mm, "construction": true});
            skLineSegment(sketch, "E182", {"start": v(0, 0) * mm, "end": v(0, 669.75) * mm, "construction": true});
            skLineSegment(sketch, "E183.rect.bottom", {"start": v(25.4, 541.94) * mm, "end": v(-25.4, 541.94) * mm, "construction": true});
            skLineSegment(sketch, "E183.rect.top", {"start": v(25.4, 625.87) * mm, "end": v(-25.4, 625.87) * mm, "construction": true});
            skLineSegment(sketch, "E183.rect.left", {"start": v(25.4, 541.94) * mm, "end": v(25.4, 625.87) * mm, "construction": true});
            skLineSegment(sketch, "E183.rect.right", {"start": v(-25.4, 541.94) * mm, "end": v(-25.4, 625.87) * mm, "construction": true});
            skPoint(sketch, "E183.rect.middle", {"position": v(0, 583.9) * mm});
            skCircle(sketch, "E184", {"center": v(0, 583.9) * mm, "radius": 4.76 * mm});
            skSolve(sketch);
        }
        {
            var Q0;
            Q0=qCreatedBy(id+"F8.planeOp",FACE);
            var sketch = newSketch(context, id + "F31", { "sketchPlane" : qUnion([Q0])});
            skLineSegment(sketch, "E185", {"start": v(285.75, 0) * mm, "end": v(-44.45, 0) * mm, "construction": true});
            skLineSegment(sketch, "E186", {"start": v(-44.45, 0) * mm, "end": v(-44.45, 838.2) * mm, "construction": true});
            skLineSegment(sketch, "E187", {"start": v(-44.45, 838.2) * mm, "end": v(285.75, 88.9) * mm, "construction": true});
            skLineSegment(sketch, "E188", {"start": v(285.75, 88.9) * mm, "end": v(285.75, 0) * mm, "construction": true});
            skLineSegment(sketch, "E189", {"start": v(285.75, 0) * mm, "end": v(374.65, 0) * mm, "construction": true});
            skLineSegment(sketch, "E190", {"start": v(202, 499.4) * mm, "end": v(-44.45, 1058.65) * mm, "construction": true});
            skLineSegment(sketch, "E191", {"start": v(-44.45, 838.2) * mm, "end": v(-44.45, 1058.65) * mm});
            skLineSegment(sketch, "E192", {"start": v(-44.45, 1058.65) * mm, "end": v(382.9, 88.9) * mm});
            skLineSegment(sketch, "E193", {"start": v(382.9, 88.9) * mm, "end": v(285.75, 88.9) * mm});
            skLineSegment(sketch, "E194", {"start": v(285.75, 88.9) * mm, "end": v(-44.45, 838.2) * mm});
            skLineSegment(sketch, "E195", {"start": v(-44.45, 948.43) * mm, "end": v(334.32, 88.9) * mm, "construction": true});
            skLineSegment(sketch, "E196", {"start": v(0, 0) * mm, "end": v(0, 957.79) * mm, "construction": true});
            skLineSegment(sketch, "E197.rect.bottom", {"start": v(25.4, 789.92) * mm, "end": v(-25.4, 789.92) * mm, "construction": true});
            skLineSegment(sketch, "E197.rect.top", {"start": v(25.4, 905.2) * mm, "end": v(-25.4, 905.2) * mm, "construction": true});
            skLineSegment(sketch, "E197.rect.left", {"start": v(25.4, 789.92) * mm, "end": v(25.4, 905.2) * mm, "construction": true});
            skLineSegment(sketch, "E197.rect.right", {"start": v(-25.4, 789.92) * mm, "end": v(-25.4, 905.2) * mm, "construction": true});
            skPoint(sketch, "E197.rect.middle", {"position": v(0, 847.56) * mm});
            skCircle(sketch, "E198", {"center": v(0, 847.56) * mm, "radius": 4.76 * mm});
            skSolve(sketch);
        }
        {
            var Q0;
            Q0=qCreatedBy(makeId("Front.planeOp"),FACE);
            var sketch = newSketch(context, id + "F32", { "sketchPlane" : qUnion([Q0])});
            skLineSegment(sketch, "E199", {"start": v(285.75, 0) * mm, "end": v(-44.45, 0) * mm, "construction": true});
            skLineSegment(sketch, "E200", {"start": v(-44.45, 0) * mm, "end": v(-44.45, 838.2) * mm, "construction": true});
            skLineSegment(sketch, "E201", {"start": v(-44.45, 838.2) * mm, "end": v(285.75, 88.9) * mm, "construction": true});
            skLineSegment(sketch, "E202", {"start": v(285.75, 88.9) * mm, "end": v(285.75, 0) * mm, "construction": true});
            skLineSegment(sketch, "E203", {"start": v(285.75, 0) * mm, "end": v(374.65, 0) * mm, "construction": true});
            skLineSegment(sketch, "E204", {"start": v(202, 499.4) * mm, "end": v(-44.45, 1058.65) * mm, "construction": true});
            skLineSegment(sketch, "E205", {"start": v(-44.45, 838.2) * mm, "end": v(-44.45, 1058.65) * mm, "construction": true});
            skLineSegment(sketch, "E206", {"start": v(-44.45, 1058.65) * mm, "end": v(382.9, 88.9) * mm, "construction": true});
            skLineSegment(sketch, "E207", {"start": v(382.9, 88.9) * mm, "end": v(285.75, 88.9) * mm, "construction": true});
            skLineSegment(sketch, "E208", {"start": v(285.75, 88.9) * mm, "end": v(-44.45, 838.2) * mm, "construction": true});
            skLineSegment(sketch, "E209", {"start": v(-44.45, 948.43) * mm, "end": v(334.32, 88.9) * mm, "construction": true});
            skLineSegment(sketch, "E210", {"start": v(0, 0) * mm, "end": v(0, 957.79) * mm, "construction": true});
            skLineSegment(sketch, "E211.rect.bottom", {"start": v(25.4, 789.92) * mm, "end": v(-25.4, 789.92) * mm, "construction": true});
            skLineSegment(sketch, "E211.rect.top", {"start": v(25.4, 905.2) * mm, "end": v(-25.4, 905.2) * mm, "construction": true});
            skLineSegment(sketch, "E211.rect.left", {"start": v(25.4, 789.92) * mm, "end": v(25.4, 905.2) * mm, "construction": true});
            skLineSegment(sketch, "E211.rect.right", {"start": v(-25.4, 789.92) * mm, "end": v(-25.4, 905.2) * mm, "construction": true});
            skPoint(sketch, "E211.rect.middle", {"position": v(0, 847.56) * mm});
            skCircle(sketch, "E212", {"center": v(-25.4, 905.2) * mm, "radius": 4.76 * mm, "construction": true});
            skCircle(sketch, "E213", {"center": v(25.4, 905.2) * mm, "radius": 4.76 * mm, "construction": true});
            skCircle(sketch, "E214", {"center": v(25.4, 789.92) * mm, "radius": 4.76 * mm, "construction": true});
            skCircle(sketch, "E215", {"center": v(-25.4, 789.92) * mm, "radius": 4.76 * mm, "construction": true});
            skCircle(sketch, "E216", {"center": v(0, 847.56) * mm, "radius": 4.76 * mm});
            skSolve(sketch);
        }
        {
            var Q0;
            Q0=qCreatedBy(id+"F12.planeOp",FACE);
            var sketch = newSketch(context, id + "F33", { "sketchPlane" : qUnion([Q0])});
            skCircle(sketch, "E217", {"center": v(0, 0) * mm, "radius": 4.76 * mm});
            skSolve(sketch);
        }
        {
            var Q0;
            Q0=qCreatedBy(id+"F12.planeOp",FACE);
            var sketch = newSketch(context, id + "F34", { "sketchPlane" : qUnion([Q0])});
            skCircle(sketch, "E218", {"center": v(0, 0) * mm, "radius": 7.14 * mm, "construction": true});
            skLineSegment(sketch, "E219", {"start": v(0, 7.14) * mm, "end": v(0, -7.14) * mm, "construction": true});
            skLineSegment(sketch, "E220", {"start": v(3.57, -6.19) * mm, "end": v(-3.57, -6.19) * mm});
            skLineSegment(sketch, "E221", {"start": v(-3.57, -6.19) * mm, "end": v(-7.14, 0) * mm});
            skLineSegment(sketch, "E222", {"start": v(3.57, -6.19) * mm, "end": v(7.14, 0) * mm});
            skLineSegment(sketch, "E223", {"start": v(-7.14, 0) * mm, "end": v(7.14, 0) * mm, "construction": true});
            skLineSegment(sketch, "E224.MirrorCS", {"start": v(3.57, 6.19) * mm, "end": v(7.14, 0) * mm});
            skLineSegment(sketch, "E225.MirrorCS", {"start": v(-3.57, 6.19) * mm, "end": v(-7.14, 0) * mm});
            skLineSegment(sketch, "E226.MirrorCS", {"start": v(3.57, 6.19) * mm, "end": v(-3.57, 6.19) * mm});
            skSolve(sketch);
        }
        {
            var Q0;
            Q0=qCreatedBy(id+"F12.planeOp",FACE);
            var sketch = newSketch(context, id + "F35", { "sketchPlane" : qUnion([Q0])});
            skCircle(sketch, "E227", {"center": v(0, 0) * mm, "radius": 5.16 * mm});
            skCircle(sketch, "E228", {"center": v(0, 0) * mm, "radius": 11.11 * mm});
            skSolve(sketch);
        }
        {
            var Q0;
            Q0=qCreatedBy(id+"F13.planeOp",FACE);
            var sketch = newSketch(context, id + "F36", { "sketchPlane" : qUnion([Q0])});
            skCircle(sketch, "E229", {"center": v(0, 0) * mm, "radius": 7.14 * mm, "construction": true});
            skLineSegment(sketch, "E230", {"start": v(-7.06, 1.11) * mm, "end": v(-7.06, -1.11) * mm, "construction": true});
            skLineSegment(sketch, "E231", {"start": v(3.57, -6.19) * mm, "end": v(-3.57, -6.19) * mm});
            skLineSegment(sketch, "E232", {"start": v(-3.57, -6.19) * mm, "end": v(-7.14, 0) * mm});
            skLineSegment(sketch, "E233", {"start": v(3.57, -6.19) * mm, "end": v(7.14, 0) * mm});
            skLineSegment(sketch, "E234", {"start": v(-7.14, 0) * mm, "end": v(7.14, 0) * mm, "construction": true});
            skLineSegment(sketch, "E235.MirrorCS", {"start": v(3.57, 6.19) * mm, "end": v(7.14, 0) * mm});
            skLineSegment(sketch, "E236.MirrorCS", {"start": v(-3.57, 6.19) * mm, "end": v(-7.14, 0) * mm});
            skLineSegment(sketch, "E237.MirrorCS", {"start": v(3.57, 6.19) * mm, "end": v(-3.57, 6.19) * mm});
            skCircle(sketch, "E238", {"center": v(0, 0) * mm, "radius": 4.76 * mm});
            skSolve(sketch);
        }
        {
            var Q0;
            Q0=qCreatedBy(makeId("Front.planeOp"),FACE);
            var sketch = newSketch(context, id + "F37", { "sketchPlane" : qUnion([Q0])});
            skLineSegment(sketch, "E239.bottom", {"start": v(0, 0) * mm, "end": v(46.04, 0) * mm});
            skLineSegment(sketch, "E239.top", {"start": v(0, 127) * mm, "end": v(46.04, 127) * mm});
            skLineSegment(sketch, "E239.left", {"start": v(0, 0) * mm, "end": v(0, 127) * mm});
            skLineSegment(sketch, "E239.right", {"start": v(46.04, 0) * mm, "end": v(46.04, 127) * mm});
            skLineSegment(sketch, "E240", {"start": v(23.02, 0) * mm, "end": v(23.02, 127) * mm, "construction": true});
            skCircle(sketch, "E241", {"center": v(23.02, 114.3) * mm, "radius": 4.76 * mm});
            skCircle(sketch, "E242", {"center": v(23.02, 12.7) * mm, "radius": 4.76 * mm});
            skSolve(sketch);
        }
        {
            var Q0;
            Q0=qCreatedBy(makeId("Front.planeOp"),FACE);
            var sketch = newSketch(context, id + "F38", { "sketchPlane" : qUnion([Q0])});
            skLineSegment(sketch, "E243", {"start": v(0, 0) * mm, "end": v(-44.45, 0) * mm, "construction": true});
            skLineSegment(sketch, "E244", {"start": v(-44.45, 0) * mm, "end": v(-44.45, 304.8) * mm, "construction": true});
            skLineSegment(sketch, "E245", {"start": v(-44.45, 0) * mm, "end": v(260.35, 0) * mm, "construction": true});
            skLineSegment(sketch, "E246", {"start": v(260.35, 0) * mm, "end": v(171.45, 0) * mm, "construction": true});
            skLineSegment(sketch, "E247", {"start": v(171.45, 0) * mm, "end": v(171.45, 88.9) * mm, "construction": true});
            skLineSegment(sketch, "E248", {"start": v(171.45, 88.9) * mm, "end": v(-44.45, 304.8) * mm, "construction": true});
            skLineSegment(sketch, "E249", {"start": v(-44.45, 304.8) * mm, "end": v(-44.45, 430.52) * mm, "construction": true});
            skLineSegment(sketch, "E250", {"start": v(-44.45, 430.52) * mm, "end": v(297.17, 88.9) * mm, "construction": true});
            skLineSegment(sketch, "E251", {"start": v(297.17, 88.9) * mm, "end": v(171.45, 88.9) * mm, "construction": true});
            skLineSegment(sketch, "E252", {"start": v(-44.45, 367.66) * mm, "end": v(234.31, 88.9) * mm, "construction": true});
            skLineSegment(sketch, "E253", {"start": v(0, 0) * mm, "end": v(0, 386.07) * mm, "construction": true});
            skPoint(sketch, "E254.rect.middle", {"position": v(0, 323.21) * mm});
            skCircle(sketch, "E255", {"center": v(0, 323.21) * mm, "radius": 4.76 * mm, "construction": true});
            skLineSegment(sketch, "E256", {"start": v(234.31, 88.9) * mm, "end": v(198.4, 124.82) * mm, "construction": true});
            skCircle(sketch, "E257", {"center": v(198.4, 124.82) * mm, "radius": 4.76 * mm});
            skSolve(sketch);
        }
        {
            var Q0;
            Q0=qCreatedBy(makeId("Front.planeOp"),FACE);
            var sketch = newSketch(context, id + "F39", { "sketchPlane" : qUnion([Q0])});
            skLineSegment(sketch, "E258", {"start": v(0, 0) * mm, "end": v(-44.45, 0) * mm, "construction": true});
            skLineSegment(sketch, "E259", {"start": v(-44.45, 0) * mm, "end": v(-44.45, 304.8) * mm, "construction": true});
            skLineSegment(sketch, "E260", {"start": v(-44.45, 0) * mm, "end": v(260.35, 0) * mm, "construction": true});
            skLineSegment(sketch, "E261", {"start": v(260.35, 0) * mm, "end": v(171.45, 0) * mm, "construction": true});
            skLineSegment(sketch, "E262", {"start": v(171.45, 0) * mm, "end": v(171.45, 88.9) * mm, "construction": true});
            skLineSegment(sketch, "E263", {"start": v(171.45, 88.9) * mm, "end": v(-44.45, 304.8) * mm, "construction": true});
            skLineSegment(sketch, "E264", {"start": v(-44.45, 304.8) * mm, "end": v(-44.45, 430.52) * mm, "construction": true});
            skLineSegment(sketch, "E265", {"start": v(-44.45, 430.52) * mm, "end": v(297.17, 88.9) * mm, "construction": true});
            skLineSegment(sketch, "E266", {"start": v(297.17, 88.9) * mm, "end": v(171.45, 88.9) * mm, "construction": true});
            skLineSegment(sketch, "E267", {"start": v(-44.45, 367.66) * mm, "end": v(234.31, 88.9) * mm, "construction": true});
            skLineSegment(sketch, "E268", {"start": v(0, 0) * mm, "end": v(0, 386.07) * mm, "construction": true});
            skPoint(sketch, "E269.rect.middle", {"position": v(0, 323.21) * mm});
            skCircle(sketch, "E270", {"center": v(0, 323.21) * mm, "radius": 4.76 * mm, "construction": true});
            skLineSegment(sketch, "E271", {"start": v(234.31, 88.9) * mm, "end": v(270.23, 52.98) * mm, "construction": true});
            skCircle(sketch, "E272", {"center": v(270.23, 52.98) * mm, "radius": 4.76 * mm});
            skSolve(sketch);
        }
        {
            var Q0;
            Q0=qCreatedBy(makeId("Front.planeOp"),FACE);
            var sketch = newSketch(context, id + "F40", { "sketchPlane" : qUnion([Q0])});
            skLineSegment(sketch, "E273", {"start": v(0, 0) * mm, "end": v(-44.45, 0) * mm, "construction": true});
            skLineSegment(sketch, "E274", {"start": v(-44.45, 0) * mm, "end": v(-44.45, 304.8) * mm, "construction": true});
            skLineSegment(sketch, "E275", {"start": v(-44.45, 0) * mm, "end": v(260.35, 0) * mm, "construction": true});
            skLineSegment(sketch, "E276", {"start": v(260.35, 0) * mm, "end": v(171.45, 0) * mm, "construction": true});
            skLineSegment(sketch, "E277", {"start": v(171.45, 0) * mm, "end": v(171.45, 88.9) * mm, "construction": true});
            skLineSegment(sketch, "E278", {"start": v(171.45, 88.9) * mm, "end": v(-44.45, 304.8) * mm, "construction": true});
            skLineSegment(sketch, "E279", {"start": v(-44.45, 304.8) * mm, "end": v(-44.45, 430.52) * mm, "construction": true});
            skLineSegment(sketch, "E280", {"start": v(-44.45, 430.52) * mm, "end": v(297.17, 88.9) * mm, "construction": true});
            skLineSegment(sketch, "E281", {"start": v(297.17, 88.9) * mm, "end": v(171.45, 88.9) * mm, "construction": true});
            skLineSegment(sketch, "E282", {"start": v(-44.45, 367.66) * mm, "end": v(234.31, 88.9) * mm, "construction": true});
            skLineSegment(sketch, "E283", {"start": v(0, 0) * mm, "end": v(0, 386.07) * mm, "construction": true});
            skPoint(sketch, "E284.rect.middle", {"position": v(0, 323.21) * mm});
            skCircle(sketch, "E285", {"center": v(0, 323.21) * mm, "radius": 4.76 * mm, "construction": true});
            skLineSegment(sketch, "E286", {"start": v(234.31, 88.9) * mm, "end": v(270.23, 52.98) * mm, "construction": true});
            skCircle(sketch, "E287", {"center": v(270.23, 52.98) * mm, "radius": 4.76 * mm, "construction": true});
            skLineSegment(sketch, "E288", {"start": v(416.1, 44.45) * mm, "end": v(-319.98, 44.45) * mm, "construction": true});
            skPoint(sketch, "E288.startSnap0", {"position": v(171.45, 44.45) * mm});
            skCircle(sketch, "E289.MirrorC", {"center": v(270.23, 35.92) * mm, "radius": 4.76 * mm});
            skSolve(sketch);
        }
        {
            var Q0;
            Q0=qCreatedBy(makeId("Right.planeOp"),FACE);
            var sketch = newSketch(context, id + "F41", { "sketchPlane" : qUnion([Q0])});
            skLineSegment(sketch, "E290", {"start": v(95.25, 0) * mm, "end": v(-44.45, 0) * mm, "construction": true});
            skLineSegment(sketch, "E291", {"start": v(-44.45, 0) * mm, "end": v(-44.45, 228.6) * mm, "construction": true});
            skLineSegment(sketch, "E292", {"start": v(-44.45, 228.6) * mm, "end": v(95.25, 88.9) * mm, "construction": true});
            skLineSegment(sketch, "E293", {"start": v(95.25, 88.9) * mm, "end": v(95.25, 0) * mm, "construction": true});
            skLineSegment(sketch, "E294", {"start": v(95.25, 0) * mm, "end": v(184.15, 0) * mm, "construction": true});
            skLineSegment(sketch, "E295", {"start": v(201.17, 108.7) * mm, "end": v(-44.45, 354.32) * mm, "construction": true});
            skLineSegment(sketch, "E296", {"start": v(-44.45, 228.6) * mm, "end": v(-44.45, 354.32) * mm, "construction": true});
            skLineSegment(sketch, "E297", {"start": v(-44.45, 354.32) * mm, "end": v(220.97, 88.9) * mm, "construction": true});
            skLineSegment(sketch, "E298", {"start": v(220.97, 88.9) * mm, "end": v(95.25, 88.9) * mm, "construction": true});
            skLineSegment(sketch, "E299", {"start": v(95.25, 88.9) * mm, "end": v(-44.45, 228.6) * mm, "construction": true});
            skLineSegment(sketch, "E300", {"start": v(-44.45, 291.46) * mm, "end": v(158.11, 88.9) * mm, "construction": true});
            skLineSegment(sketch, "E301", {"start": v(0, 0) * mm, "end": v(0, 309.87) * mm, "construction": true});
            skLineSegment(sketch, "E302.rect.bottom", {"start": v(25.4, 221.61) * mm, "end": v(-25.4, 221.61) * mm, "construction": true});
            skLineSegment(sketch, "E302.rect.top", {"start": v(25.4, 272.41) * mm, "end": v(-25.4, 272.41) * mm, "construction": true});
            skLineSegment(sketch, "E302.rect.left", {"start": v(25.4, 221.61) * mm, "end": v(25.4, 272.41) * mm, "construction": true});
            skLineSegment(sketch, "E302.rect.right", {"start": v(-25.4, 221.61) * mm, "end": v(-25.4, 272.41) * mm, "construction": true});
            skPoint(sketch, "E302.rect.middle", {"position": v(0, 247.01) * mm});
            skCircle(sketch, "E303", {"center": v(0, 247.01) * mm, "radius": 4.76 * mm, "construction": true});
            skLineSegment(sketch, "E304", {"start": v(158.11, 88.9) * mm, "end": v(122.2, 124.82) * mm, "construction": true});
            skCircle(sketch, "E305", {"center": v(122.2, 124.82) * mm, "radius": 4.76 * mm});
            skSolve(sketch);
        }
        {
            var Q0;
            Q0=qCreatedBy(makeId("Right.planeOp"),FACE);
            var sketch = newSketch(context, id + "F42", { "sketchPlane" : qUnion([Q0])});
            skLineSegment(sketch, "E306", {"start": v(95.25, 0) * mm, "end": v(-44.45, 0) * mm, "construction": true});
            skLineSegment(sketch, "E307", {"start": v(-44.45, 0) * mm, "end": v(-44.45, 228.6) * mm, "construction": true});
            skLineSegment(sketch, "E308", {"start": v(-44.45, 228.6) * mm, "end": v(95.25, 88.9) * mm, "construction": true});
            skLineSegment(sketch, "E309", {"start": v(95.25, 88.9) * mm, "end": v(95.25, 0) * mm, "construction": true});
            skLineSegment(sketch, "E310", {"start": v(95.25, 0) * mm, "end": v(184.15, 0) * mm, "construction": true});
            skLineSegment(sketch, "E311", {"start": v(201.17, 108.7) * mm, "end": v(-44.45, 354.32) * mm, "construction": true});
            skLineSegment(sketch, "E312", {"start": v(-44.45, 228.6) * mm, "end": v(-44.45, 354.32) * mm, "construction": true});
            skLineSegment(sketch, "E313", {"start": v(-44.45, 354.32) * mm, "end": v(220.97, 88.9) * mm, "construction": true});
            skLineSegment(sketch, "E314", {"start": v(220.97, 88.9) * mm, "end": v(95.25, 88.9) * mm, "construction": true});
            skLineSegment(sketch, "E315", {"start": v(95.25, 88.9) * mm, "end": v(-44.45, 228.6) * mm, "construction": true});
            skLineSegment(sketch, "E316", {"start": v(-44.45, 291.46) * mm, "end": v(158.11, 88.9) * mm, "construction": true});
            skLineSegment(sketch, "E317", {"start": v(0, 0) * mm, "end": v(0, 309.87) * mm, "construction": true});
            skLineSegment(sketch, "E318.rect.bottom", {"start": v(25.4, 221.61) * mm, "end": v(-25.4, 221.61) * mm, "construction": true});
            skLineSegment(sketch, "E318.rect.top", {"start": v(25.4, 272.41) * mm, "end": v(-25.4, 272.41) * mm, "construction": true});
            skLineSegment(sketch, "E318.rect.left", {"start": v(25.4, 221.61) * mm, "end": v(25.4, 272.41) * mm, "construction": true});
            skLineSegment(sketch, "E318.rect.right", {"start": v(-25.4, 221.61) * mm, "end": v(-25.4, 272.41) * mm, "construction": true});
            skPoint(sketch, "E318.rect.middle", {"position": v(0, 247.01) * mm});
            skCircle(sketch, "E319", {"center": v(0, 247.01) * mm, "radius": 4.76 * mm, "construction": true});
            skLineSegment(sketch, "E320", {"start": v(158.11, 88.9) * mm, "end": v(122.2, 124.82) * mm, "construction": true});
            skCircle(sketch, "E321", {"center": v(122.2, 124.82) * mm, "radius": 4.76 * mm, "construction": true});
            skLineSegment(sketch, "E322", {"start": v(158.11, 88.9) * mm, "end": v(194.03, 52.98) * mm, "construction": true});
            skCircle(sketch, "E323", {"center": v(194.03, 52.98) * mm, "radius": 4.76 * mm});
            skSolve(sketch);
        }
        {
            var Q0;
            Q0 = qSketchRegion(id + "F15", true);
            extrude(context, id + "F43", {"entities" : qUnion([Q0]), "depth" : getVariable(context, 'msc6')});
        }
        {
            var Q0;
            Q0 = qSketchRegion(id + "F16", true);
            extrude(context, id + "F44", {"entities" : qUnion([Q0]), "operationType" : NewBodyOperationType.REMOVE, "endBound" : BoundingType.THROUGH_ALL, "oppositeDirection" : true, "depth" : 25.4 * mm});
        }
        {
            var Q0;
            Q0 = qSketchRegion(id + "F17", true);
            extrude(context, id + "F45", {"entities" : qUnion([Q0]), "operationType" : NewBodyOperationType.REMOVE, "endBound" : BoundingType.THROUGH_ALL, "oppositeDirection" : true, "depth" : 25.4 * mm});
        }
        {
            var Q0;
            Q0 = qSketchRegion(id + "F15", true);
            extrude(context, id + "F46", {"entities" : qUnion([Q0]), "depth" : getVariable(context, 'msc18')});
        }
        {
            var Q0;
            Q0 = qSketchRegion(id + "F16", true);
            extrude(context, id + "F47", {"entities" : qUnion([Q0]), "operationType" : NewBodyOperationType.REMOVE, "endBound" : BoundingType.THROUGH_ALL, "oppositeDirection" : true, "depth" : 25.4 * mm});
        }
        {
            var Q0;
            Q0 = qSketchRegion(id + "F17", true);
            extrude(context, id + "F48", {"entities" : qUnion([Q0]), "operationType" : NewBodyOperationType.REMOVE, "endBound" : BoundingType.THROUGH_ALL, "oppositeDirection" : true, "depth" : 25.4 * mm});
        }
        {
            var Q0;
            Q0 = qSketchRegion(id + "F25", true);
            extrude(context, id + "F49", {"entities" : qUnion([Q0]), "operationType" : NewBodyOperationType.REMOVE, "endBound" : BoundingType.THROUGH_ALL, "oppositeDirection" : true, "depth" : 25.4 * mm, "hasSecondDirection" : true, "secondDirectionBound" : SecondDirectionBoundingType.THROUGH_ALL, "secondDirectionOppositeDirection" : false, "secondDirectionDepth" : 25.4 * mm});
        }
        {
            var Q0;
            Q0 = qSketchRegion(id + "F26", true);
            extrude(context, id + "F50", {"entities" : qUnion([Q0]), "operationType" : NewBodyOperationType.REMOVE, "endBound" : BoundingType.THROUGH_ALL, "oppositeDirection" : true, "depth" : 25.4 * mm, "hasSecondDirection" : true, "secondDirectionBound" : SecondDirectionBoundingType.THROUGH_ALL, "secondDirectionOppositeDirection" : false, "secondDirectionDepth" : 25.4 * mm});
        }
        {
            var Q0;
            Q0 = qSketchRegion(id + "F15", true);
            extrude(context, id + "F51", {"entities" : qUnion([Q0]), "depth" : getVariable(context, 'msc24')});
        }
        {
            var Q0;
            Q0 = qSketchRegion(id + "F16", true);
            extrude(context, id + "F52", {"entities" : qUnion([Q0]), "operationType" : NewBodyOperationType.REMOVE, "endBound" : BoundingType.THROUGH_ALL, "oppositeDirection" : true, "depth" : 25.4 * mm});
        }
        {
            var Q0;
            Q0 = qSketchRegion(id + "F17", true);
            extrude(context, id + "F53", {"entities" : qUnion([Q0]), "operationType" : NewBodyOperationType.REMOVE, "endBound" : BoundingType.THROUGH_ALL, "oppositeDirection" : true, "depth" : 25.4 * mm});
        }
        {
            var Q0;
            Q0 = qSketchRegion(id + "F25", true);
            extrude(context, id + "F54", {"entities" : qUnion([Q0]), "operationType" : NewBodyOperationType.REMOVE, "endBound" : BoundingType.THROUGH_ALL, "oppositeDirection" : true, "depth" : 25.4 * mm, "hasSecondDirection" : true, "secondDirectionBound" : SecondDirectionBoundingType.THROUGH_ALL, "secondDirectionOppositeDirection" : false, "secondDirectionDepth" : 25.4 * mm});
        }
        {
            var Q0;
            Q0 = qSketchRegion(id + "F26", true);
            extrude(context, id + "F55", {"entities" : qUnion([Q0]), "operationType" : NewBodyOperationType.REMOVE, "endBound" : BoundingType.THROUGH_ALL, "oppositeDirection" : true, "depth" : 25.4 * mm, "hasSecondDirection" : true, "secondDirectionBound" : SecondDirectionBoundingType.THROUGH_ALL, "secondDirectionOppositeDirection" : false, "secondDirectionDepth" : 25.4 * mm});
        }
        {
            var Q0;
            Q0 = qSketchRegion(id + "F15", true);
            extrude(context, id + "F56", {"entities" : qUnion([Q0]), "depth" : getVariable(context, 'msc30')});
        }
        {
            var Q0;
            Q0 = qSketchRegion(id + "F16", true);
            extrude(context, id + "F57", {"entities" : qUnion([Q0]), "operationType" : NewBodyOperationType.REMOVE, "endBound" : BoundingType.THROUGH_ALL, "oppositeDirection" : true, "depth" : 25.4 * mm});
        }
        {
            var Q0;
            Q0 = qSketchRegion(id + "F17", true);
            extrude(context, id + "F58", {"entities" : qUnion([Q0]), "operationType" : NewBodyOperationType.REMOVE, "endBound" : BoundingType.THROUGH_ALL, "oppositeDirection" : true, "depth" : 25.4 * mm});
        }
        {
            var Q0;
            Q0 = qSketchRegion(id + "F28", true);
            extrude(context, id + "F59", {"entities" : qUnion([Q0]), "operationType" : NewBodyOperationType.REMOVE, "endBound" : BoundingType.THROUGH_ALL, "oppositeDirection" : true, "depth" : 25.4 * mm, "hasSecondDirection" : true, "secondDirectionBound" : SecondDirectionBoundingType.THROUGH_ALL, "secondDirectionOppositeDirection" : false, "secondDirectionDepth" : 25.4 * mm});
        }
        {
            var Q0;
            Q0 = qSketchRegion(id + "F21", true);
            extrude(context, id + "F60", {"entities" : qUnion([Q0]), "operationType" : NewBodyOperationType.REMOVE, "endBound" : BoundingType.THROUGH_ALL, "oppositeDirection" : true, "depth" : 25.4 * mm, "hasSecondDirection" : true, "secondDirectionBound" : SecondDirectionBoundingType.THROUGH_ALL, "secondDirectionOppositeDirection" : false, "secondDirectionDepth" : 25.4 * mm});
        }
        {
            var Q0;
            Q0 = qSketchRegion(id + "F15", true);
            extrude(context, id + "F61", {"entities" : qUnion([Q0]), "depth" : getVariable(context, 'msc45')});
        }
        {
            var Q0;
            Q0 = qSketchRegion(id + "F16", true);
            extrude(context, id + "F62", {"entities" : qUnion([Q0]), "operationType" : NewBodyOperationType.REMOVE, "endBound" : BoundingType.THROUGH_ALL, "oppositeDirection" : true, "depth" : 25.4 * mm});
        }
        {
            var Q0;
            Q0 = qSketchRegion(id + "F17", true);
            extrude(context, id + "F63", {"entities" : qUnion([Q0]), "operationType" : NewBodyOperationType.REMOVE, "endBound" : BoundingType.THROUGH_ALL, "oppositeDirection" : true, "depth" : 25.4 * mm});
        }
        {
            var Q0;
            Q0 = qSketchRegion(id + "F30", true);
            extrude(context, id + "F64", {"entities" : qUnion([Q0]), "operationType" : NewBodyOperationType.REMOVE, "endBound" : BoundingType.THROUGH_ALL, "oppositeDirection" : true, "depth" : 25.4 * mm, "hasSecondDirection" : true, "secondDirectionBound" : SecondDirectionBoundingType.THROUGH_ALL, "secondDirectionOppositeDirection" : false, "secondDirectionDepth" : 25.4 * mm});
        }
        {
            var Q0;
            Q0 = qSketchRegion(id + "F21", true);
            extrude(context, id + "F65", {"entities" : qUnion([Q0]), "operationType" : NewBodyOperationType.REMOVE, "endBound" : BoundingType.THROUGH_ALL, "oppositeDirection" : true, "depth" : 25.4 * mm, "hasSecondDirection" : true, "secondDirectionBound" : SecondDirectionBoundingType.THROUGH_ALL, "secondDirectionOppositeDirection" : false, "secondDirectionDepth" : 25.4 * mm});
        }
        {
            var Q0;
            Q0 = qSketchRegion(id + "F15", true);
            extrude(context, id + "F66", {"entities" : qUnion([Q0]), "depth" : getVariable(context, 'msc66')});
        }
        {
            var Q0;
            Q0 = qSketchRegion(id + "F16", true);
            extrude(context, id + "F67", {"entities" : qUnion([Q0]), "operationType" : NewBodyOperationType.REMOVE, "endBound" : BoundingType.THROUGH_ALL, "oppositeDirection" : true, "depth" : 25.4 * mm});
        }
        {
            var Q0;
            Q0 = qSketchRegion(id + "F17", true);
            extrude(context, id + "F68", {"entities" : qUnion([Q0]), "operationType" : NewBodyOperationType.REMOVE, "endBound" : BoundingType.THROUGH_ALL, "oppositeDirection" : true, "depth" : 25.4 * mm});
        }
        {
            var Q0;
            Q0 = qSketchRegion(id + "F32", true);
            extrude(context, id + "F69", {"entities" : qUnion([Q0]), "operationType" : NewBodyOperationType.REMOVE, "endBound" : BoundingType.THROUGH_ALL, "oppositeDirection" : true, "depth" : 25.4 * mm, "hasSecondDirection" : true, "secondDirectionBound" : SecondDirectionBoundingType.THROUGH_ALL, "secondDirectionOppositeDirection" : false, "secondDirectionDepth" : 25.4 * mm});
        }
        {
            var Q0;
            Q0 = qSketchRegion(id + "F21", true);
            extrude(context, id + "F70", {"entities" : qUnion([Q0]), "operationType" : NewBodyOperationType.REMOVE, "endBound" : BoundingType.THROUGH_ALL, "oppositeDirection" : true, "depth" : 25.4 * mm, "hasSecondDirection" : true, "secondDirectionBound" : SecondDirectionBoundingType.THROUGH_ALL, "secondDirectionOppositeDirection" : false, "secondDirectionDepth" : 25.4 * mm});
        }
        {
            var Q0;
            Q0 = qSketchRegion(id + "F18", true);
            extrude(context, id + "F71", {"entities" : qUnion([Q0]), "depth" : (getVariable(context, 'basethick')) * mm});
        }
        {
            var Q0;
            Q0=makeQuery(id+"F71.opExtrude","SWEPT_BODY",BODY,{"disambiguationData":[OSD([sQuery(id+"F18.wireOp",EDGE,"E16.bottom"),sQuery(id+"F18.wireOp",EDGE,"E16.top"),sQuery(id+"F18.wireOp",EDGE,"E16.left"),sQuery(id+"F18.wireOp",EDGE,"E16.right"),sQuery(id+"F18.wireOp",EDGE,"E20"),sQuery(id+"F18.wireOp",EDGE,"E21")])]});
            transform(context, id + "F72", {"entities" : qUnion([Q0]), "transformType" : TransformType.COPY});
        }
        {
            var Q0;
            Q0=makeQuery(id+"F72.opPattern","COPY",BODY,{"derivedFrom":makeQuery(id+"F71.opExtrude","SWEPT_BODY",BODY,{"disambiguationData":[OSD([sQuery(id+"F18.wireOp",EDGE,"E16.bottom"),sQuery(id+"F18.wireOp",EDGE,"E16.top"),sQuery(id+"F18.wireOp",EDGE,"E16.left"),sQuery(id+"F18.wireOp",EDGE,"E16.right"),sQuery(id+"F18.wireOp",EDGE,"E20"),sQuery(id+"F18.wireOp",EDGE,"E21")])]}),"instanceName":"1"});
            transform(context, id + "F73", {"entities" : qUnion([Q0]), "transformType" : TransformType.COPY});
        }
        {
            var Q0;
            Q0=makeQuery(id+"F71.opExtrude","SWEPT_BODY",BODY,{"disambiguationData":[OSD([sQuery(id+"F18.wireOp",EDGE,"E16.bottom"),sQuery(id+"F18.wireOp",EDGE,"E16.top"),sQuery(id+"F18.wireOp",EDGE,"E16.left"),sQuery(id+"F18.wireOp",EDGE,"E16.right"),sQuery(id+"F18.wireOp",EDGE,"E20"),sQuery(id+"F18.wireOp",EDGE,"E21")])]});
            transform(context, id + "F74", {"entities" : qUnion([Q0]), "transformType" : TransformType.COPY});
        }
        {
            var Q0;
            Q0=makeQuery(id+"F71.opExtrude","SWEPT_BODY",BODY,{"disambiguationData":[OSD([sQuery(id+"F18.wireOp",EDGE,"E16.bottom"),sQuery(id+"F18.wireOp",EDGE,"E16.top"),sQuery(id+"F18.wireOp",EDGE,"E16.left"),sQuery(id+"F18.wireOp",EDGE,"E16.right"),sQuery(id+"F18.wireOp",EDGE,"E20"),sQuery(id+"F18.wireOp",EDGE,"E21")])]});
            transform(context, id + "F75", {"entities" : qUnion([Q0]), "transformType" : TransformType.COPY});
        }
        {
            var Q0;
            Q0=makeQuery(id+"F71.opExtrude","SWEPT_BODY",BODY,{"disambiguationData":[OSD([sQuery(id+"F18.wireOp",EDGE,"E16.bottom"),sQuery(id+"F18.wireOp",EDGE,"E16.top"),sQuery(id+"F18.wireOp",EDGE,"E16.left"),sQuery(id+"F18.wireOp",EDGE,"E16.right"),sQuery(id+"F18.wireOp",EDGE,"E20"),sQuery(id+"F18.wireOp",EDGE,"E21")])]});
            transform(context, id + "F76", {"entities" : qUnion([Q0]), "transformType" : TransformType.COPY});
        }
        {
            var Q0;
            Q0 = qSketchRegion(id + "F19", true);
            extrude(context, id + "F77", {"entities" : qUnion([Q0]), "depth" : (getVariable(context, 'basethick')) * mm});
        }
        {
            var Q0;
            Q0=makeQuery(id+"F77.opExtrude","SWEPT_BODY",BODY,{"disambiguationData":[OSD([sQuery(id+"F19.wireOp",EDGE,"E24.bottom"),sQuery(id+"F19.wireOp",EDGE,"E24.top"),sQuery(id+"F19.wireOp",EDGE,"E24.left"),sQuery(id+"F19.wireOp",EDGE,"E24.right"),sQuery(id+"F19.wireOp",EDGE,"E29"),sQuery(id+"F19.wireOp",EDGE,"E30")])]});
            transform(context, id + "F78", {"entities" : qUnion([Q0]), "transformType" : TransformType.COPY});
        }
        {
            var Q0;
            Q0=makeQuery(id+"F77.opExtrude","SWEPT_BODY",BODY,{"disambiguationData":[OSD([sQuery(id+"F19.wireOp",EDGE,"E24.bottom"),sQuery(id+"F19.wireOp",EDGE,"E24.top"),sQuery(id+"F19.wireOp",EDGE,"E24.left"),sQuery(id+"F19.wireOp",EDGE,"E24.right"),sQuery(id+"F19.wireOp",EDGE,"E29"),sQuery(id+"F19.wireOp",EDGE,"E30")])]});
            transform(context, id + "F79", {"entities" : qUnion([Q0]), "transformType" : TransformType.TRANSLATION_3D, "dx" : 0 * mm, "dy" : 0 * mm, "dz" : 0 * mm, "makeCopy" : true});
        }
        {
            var Q0;
            Q0 = qSketchRegion(id + "F20", true);
            extrude(context, id + "F80", {"entities" : qUnion([Q0]), "oppositeDirection" : true, "depth" : (getVariable(context, 'basethick')) * mm});
        }
        {
            var Q0;
            Q0 = qSketchRegion(id + "F23", true);
            extrude(context, id + "F81", {"entities" : qUnion([Q0]), "depth" : (getVariable(context, 'basethick')) * mm});
        }
        {
            var Q0;
            Q0 = qSketchRegion(id + "F24", true);
            extrude(context, id + "F82", {"entities" : qUnion([Q0]), "oppositeDirection" : true, "depth" : (getVariable(context, 'basethick')) * mm});
        }
        {
            var Q0;
            Q0 = qSketchRegion(id + "F27", true);
            extrude(context, id + "F83", {"entities" : qUnion([Q0]), "depth" : (getVariable(context, 'basethick')) * mm});
        }
        {
            var Q0;
            Q0 = qSketchRegion(id + "F29", true);
            extrude(context, id + "F84", {"entities" : qUnion([Q0]), "oppositeDirection" : true, "depth" : (getVariable(context, 'basethick')) * mm});
        }
        {
            var Q0;
            Q0 = qSketchRegion(id + "F31", true);
            extrude(context, id + "F85", {"entities" : qUnion([Q0]), "depth" : (getVariable(context, 'basethick')) * mm});
        }
        {
            var Q0;
            Q0 = qSketchRegion(id + "F33", true);
            extrude(context, id + "F86", {"entities" : qUnion([Q0]), "oppositeDirection" : true, "depth" : 189.21 * mm});
        }
        {
            var Q0;
            Q0 = qSketchRegion(id + "F34", true);
            extrude(context, id + "F87", {"entities" : qUnion([Q0]), "operationType" : NewBodyOperationType.ADD, "depth" : 7.8 * mm});
        }
        {
            var Q0;
            Q0=makeQuery(id+"F35.imprint","IMPRINT",FACE,{"disambiguationData":[TD([[makeQuery(id+"F35.imprint","IMPRINT",EDGE,{"derivedFrom":sQuery(id+"F35.wireOp",EDGE,"E227")}),-1.0]])]});
            extrude(context, id + "F88", {"entities" : qUnion([Q0]), "operationType" : NewBodyOperationType.ADD, "depth" : 1.45 * mm});
        }
        {
            var Q0;
            Q0=makeQuery(id+"F36.imprint","IMPRINT",FACE,{"disambiguationData":[TD([[makeQuery(id+"F36.imprint","IMPRINT",EDGE,{"derivedFrom":sQuery(id+"F36.wireOp",EDGE,"E231")}),-1.0]])]});
            extrude(context, id + "F89", {"entities" : qUnion([Q0]), "operationType" : NewBodyOperationType.ADD, "oppositeDirection" : true, "depth" : 9.78 * mm});
        }
        {
            var Q0;
            Q0 = qSketchRegion(id + "F35", true);
            extrude(context, id + "F90", {"entities" : qUnion([Q0]), "operationType" : NewBodyOperationType.ADD, "oppositeDirection" : true, "depth" : 166.55 * mm, "hasSecondDirection" : true, "secondDirectionOppositeDirection" : true, "secondDirectionDepth" : 165.1 * mm});
        }
        {
            var Q0;
            Q0 = qSketchRegion(id + "F33", true);
            extrude(context, id + "F91", {"entities" : qUnion([Q0]), "oppositeDirection" : true, "depth" : 50.8 * mm});
        }
        {
            var Q0;
            Q0 = qSketchRegion(id + "F34", true);
            extrude(context, id + "F92", {"entities" : qUnion([Q0]), "operationType" : NewBodyOperationType.ADD, "depth" : 7.8 * mm});
        }
        {
            var Q0;
            Q0 = qSketchRegion(id + "F35", true);
            extrude(context, id + "F93", {"entities" : qUnion([Q0]), "operationType" : NewBodyOperationType.ADD, "depth" : 1.45 * mm});
        }
        {
            var Q0;
            Q0 = qSketchRegion(id + "F36", true);
            extrude(context, id + "F94", {"entities" : qUnion([Q0]), "operationType" : NewBodyOperationType.ADD, "depth" : 125.1 * mm, "hasSecondDirection" : true, "secondDirectionOppositeDirection" : false, "secondDirectionDepth" : 115.32 * mm});
        }
        {
            var Q0;
            Q0 = qSketchRegion(id + "F35", true);
            extrude(context, id + "F95", {"entities" : qUnion([Q0]), "operationType" : NewBodyOperationType.ADD, "oppositeDirection" : true, "depth" : 41.45 * mm, "hasSecondDirection" : true, "secondDirectionOppositeDirection" : true, "secondDirectionDepth" : 40 * mm});
        }
        {
            var Q0;
            Q0=makeQuery(id+"F37.imprint","IMPRINT",FACE,{"disambiguationData":[TD([[makeQuery(id+"F37.imprint","IMPRINT",EDGE,{"derivedFrom":sQuery(id+"F37.wireOp",EDGE,"E239.bottom")}),1.0]])]});
            extrude(context, id + "F96", {"entities" : qUnion([Q0]), "depth" : 0.95 * mm});
        }
        {
            var Q0;
            Q0 = qSketchRegion(id + "F38", true);
            extrude(context, id + "F97", {"entities" : qUnion([Q0]), "operationType" : NewBodyOperationType.REMOVE, "endBound" : BoundingType.THROUGH_ALL, "depth" : 25.4 * mm});
        }
        {
            var Q0;
            Q0 = qSketchRegion(id + "F39", true);
            extrude(context, id + "F98", {"entities" : qUnion([Q0]), "operationType" : NewBodyOperationType.REMOVE, "endBound" : BoundingType.THROUGH_ALL, "depth" : 25.4 * mm});
        }
        {
            var Q0;
            Q0 = qSketchRegion(id + "F40", true);
            extrude(context, id + "F99", {"entities" : qUnion([Q0]), "operationType" : NewBodyOperationType.REMOVE, "endBound" : BoundingType.THROUGH_ALL, "depth" : 25.4 * mm});
        }
        {
            var Q0;
            Q0 = qSketchRegion(id + "F41", true);
            extrude(context, id + "F100", {"entities" : qUnion([Q0]), "operationType" : NewBodyOperationType.REMOVE, "endBound" : BoundingType.THROUGH_ALL, "depth" : 25.4 * mm});
        }
        {
            var Q0;
            Q0 = qSketchRegion(id + "F42", true);
            extrude(context, id + "F101", {"entities" : qUnion([Q0]), "operationType" : NewBodyOperationType.REMOVE, "endBound" : BoundingType.THROUGH_ALL, "depth" : 25.4 * mm});
        }
    });
